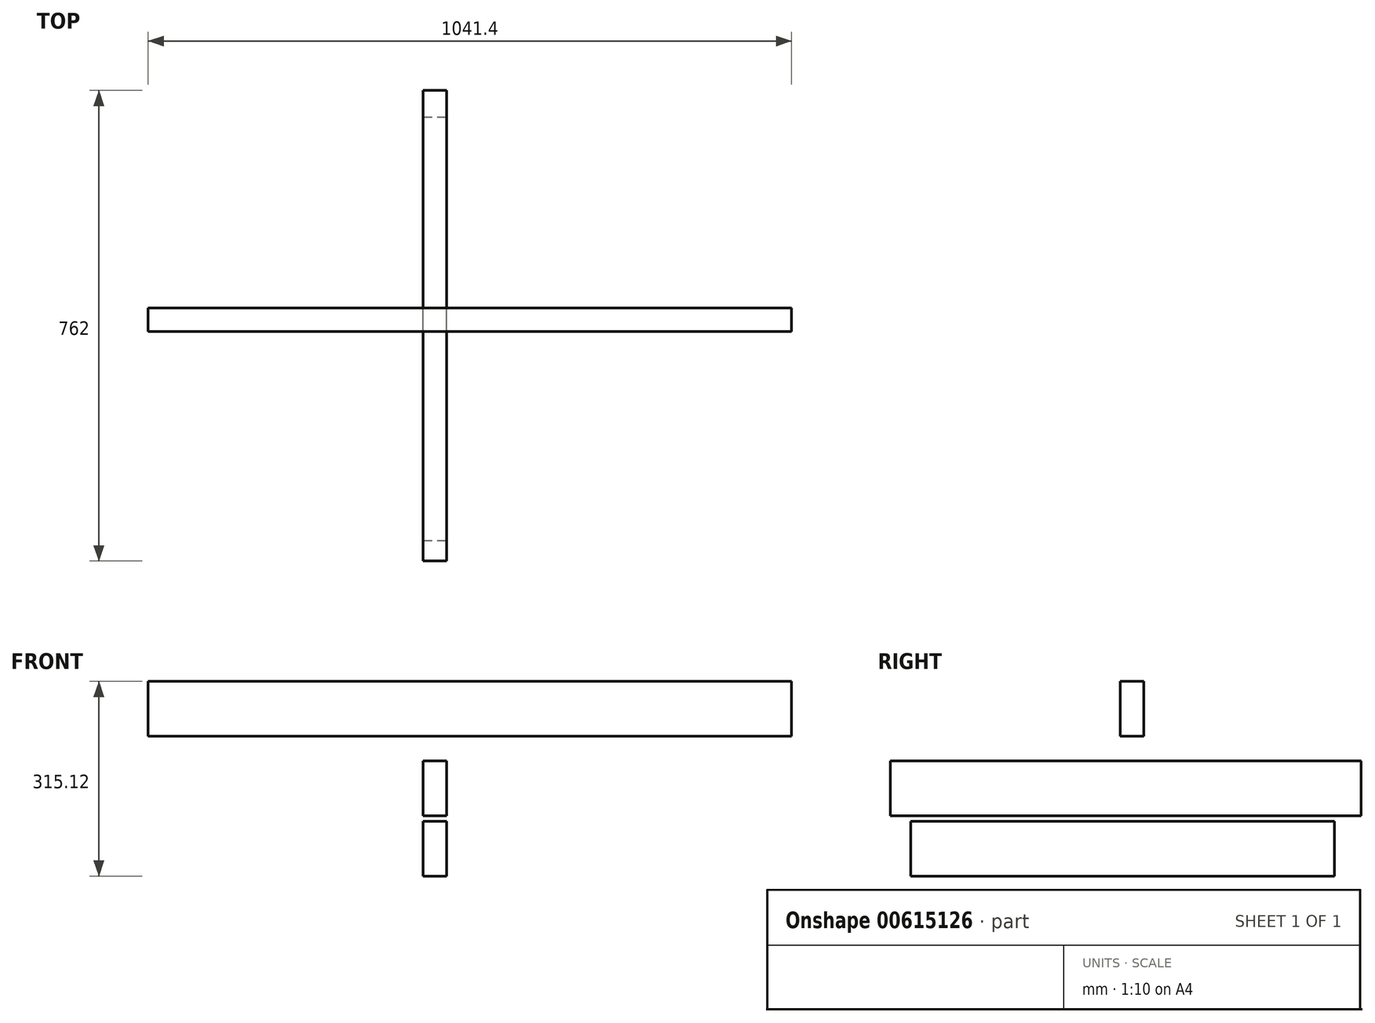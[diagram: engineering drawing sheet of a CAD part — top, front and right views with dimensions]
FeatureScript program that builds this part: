
annotation { "Feature Type Name" : "Feature", "Feature Type Description" : "" }
export const myFeature = defineFeature(function(context is Context, id is Id, definition is map)
    precondition{}
    {
        {
            var Q0;
            Q0=qCreatedBy(makeId("Front.planeOp"),FACE);
            var sketch = newSketch(context, id + "F0", { "sketchPlane" : qUnion([Q0])});
            skLineSegment(sketch, "E0.bottom", {"start": v(-444.5, 69.24) * mm, "end": v(596.9, 69.24) * mm});
            skLineSegment(sketch, "E0.top", {"start": v(-444.5, -19.66) * mm, "end": v(596.9, -19.66) * mm});
            skLineSegment(sketch, "E0.left", {"start": v(-444.5, 69.24) * mm, "end": v(-444.5, -19.66) * mm});
            skLineSegment(sketch, "E0.right", {"start": v(596.9, 69.24) * mm, "end": v(596.9, -19.66) * mm});
            skSolve(sketch);
        }
        {
            var Q0;
            Q0=makeQuery(id+"F0.imprint","IMPRINT",FACE,{"disambiguationData":[TD([[makeQuery(id+"F0.imprint","IMPRINT",EDGE,{"derivedFrom":sQuery(id+"F0.wireOp",EDGE,"E0.bottom")}),-1.0]])]});
            extrude(context, id + "F1", {"entities" : qUnion([Q0]), "depth" : 38.1 * mm});
        }
        {
            var Q0;
            Q0=qCreatedBy(makeId("Right.planeOp"),FACE);
            var sketch = newSketch(context, id + "F2", { "sketchPlane" : qUnion([Q0])});
            skLineSegment(sketch, "E1.bottom", {"start": v(-409.68, -59.62) * mm, "end": v(352.32, -59.62) * mm});
            skLineSegment(sketch, "E1.top", {"start": v(-409.68, -148.52) * mm, "end": v(352.32, -148.52) * mm});
            skLineSegment(sketch, "E1.left", {"start": v(-409.68, -59.62) * mm, "end": v(-409.68, -148.52) * mm});
            skLineSegment(sketch, "E1.right", {"start": v(352.32, -59.62) * mm, "end": v(352.32, -148.52) * mm});
            skSolve(sketch);
        }
        {
            var Q0;
            Q0=qSketchRegion(id+"F2",true);
            extrude(context, id + "F3", {"entities" : qUnion([Q0]), "depth" : 38.1 * mm});
        }
        {
            var Q0;
            Q0=qCreatedBy(makeId("Right.planeOp"),FACE);
            var sketch = newSketch(context, id + "F4", { "sketchPlane" : qUnion([Q0])});
            skLineSegment(sketch, "E2.bottom", {"start": v(-376.8, -156.98) * mm, "end": v(309, -156.98) * mm});
            skLineSegment(sketch, "E2.top", {"start": v(-376.8, -245.88) * mm, "end": v(309, -245.88) * mm});
            skLineSegment(sketch, "E2.left", {"start": v(-376.8, -156.98) * mm, "end": v(-376.8, -245.88) * mm});
            skLineSegment(sketch, "E2.right", {"start": v(309, -156.98) * mm, "end": v(309, -245.88) * mm});
            skSolve(sketch);
        }
        {
            var Q0;
            Q0=makeQuery(id+"F4.imprint","IMPRINT",FACE,{"disambiguationData":[TD([[makeQuery(id+"F4.imprint","IMPRINT",EDGE,{"derivedFrom":sQuery(id+"F4.wireOp",EDGE,"E2.bottom")}),-1.0]])]});
            extrude(context, id + "F5", {"entities" : qUnion([Q0]), "depth" : 38.1 * mm});
        }
    });
